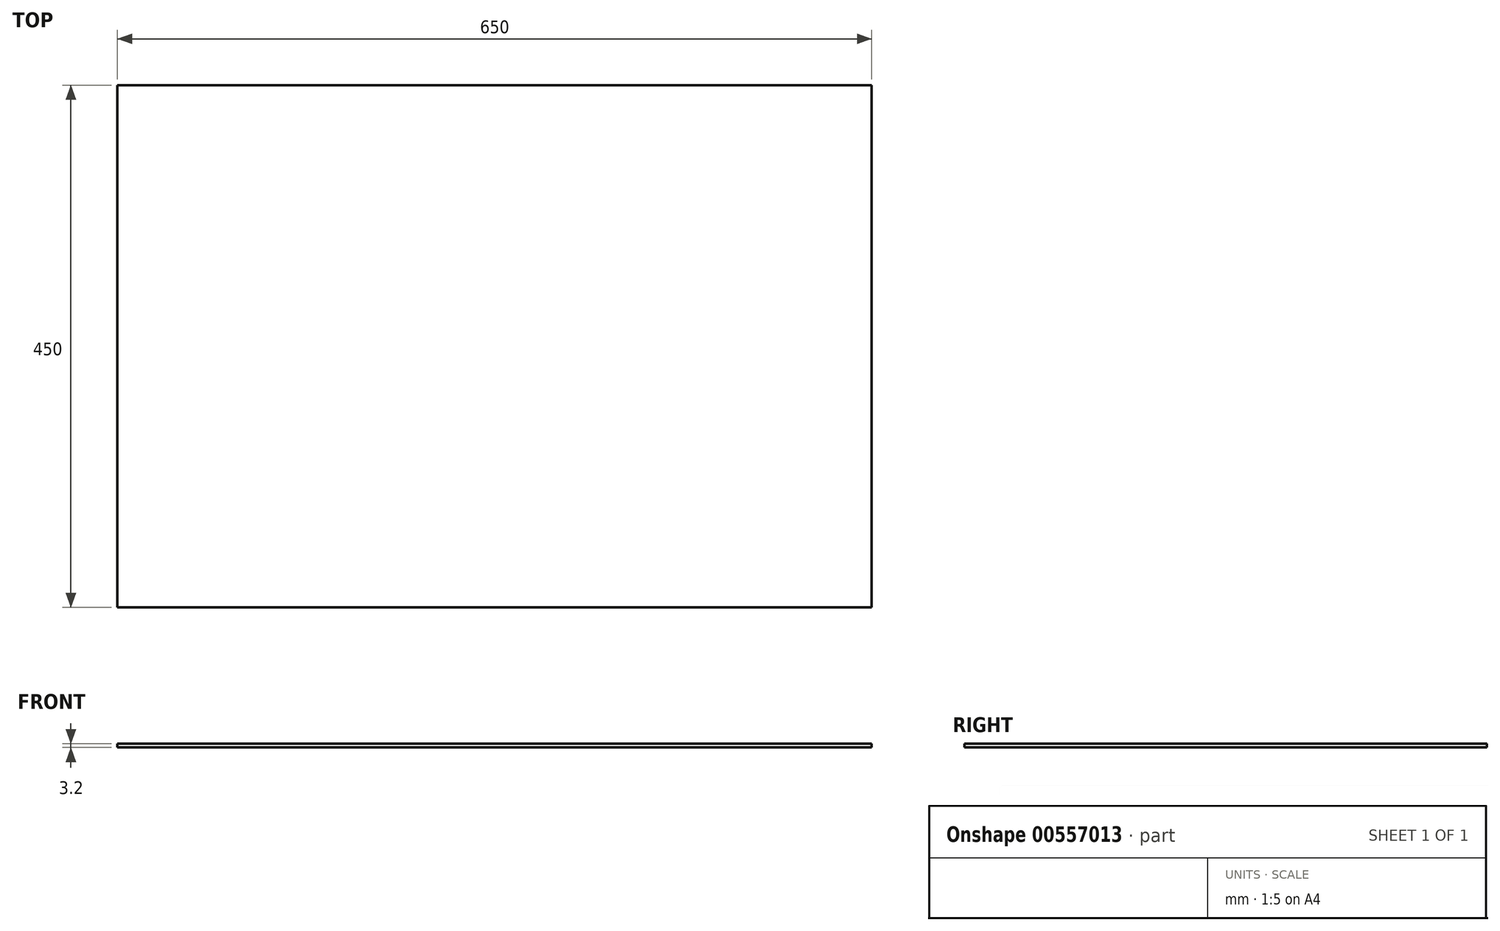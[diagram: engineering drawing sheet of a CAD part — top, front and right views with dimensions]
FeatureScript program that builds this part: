
annotation { "Feature Type Name" : "Feature", "Feature Type Description" : "" }
export const myFeature = defineFeature(function(context is Context, id is Id, definition is map)
    precondition{}
    {
        {
            var Q0;
            Q0=qCreatedBy(makeId("Top.planeOp"),FACE);
            var sketch = newSketch(context, id + "F0", { "sketchPlane" : qUnion([Q0])});
            skLineSegment(sketch, "E0.bottom", {"start": v(325, -225) * mm, "end": v(-325, -225) * mm});
            skLineSegment(sketch, "E0.top", {"start": v(325, 225) * mm, "end": v(-325, 225) * mm});
            skLineSegment(sketch, "E0.left", {"start": v(325, -225) * mm, "end": v(325, 225) * mm});
            skLineSegment(sketch, "E0.right", {"start": v(-325, -225) * mm, "end": v(-325, 225) * mm});
            skPoint(sketch, "E0.middle", {"position": v(0, 0) * mm});
            skSolve(sketch);
        }
        {
            var Q0;
            Q0=qSketchRegion(id+"F0",true);
            extrude(context, id + "F1", {"entities" : qUnion([Q0]), "depth" : 3.2 * mm, "offsetDistance" : 25 * mm});
        }
    });
